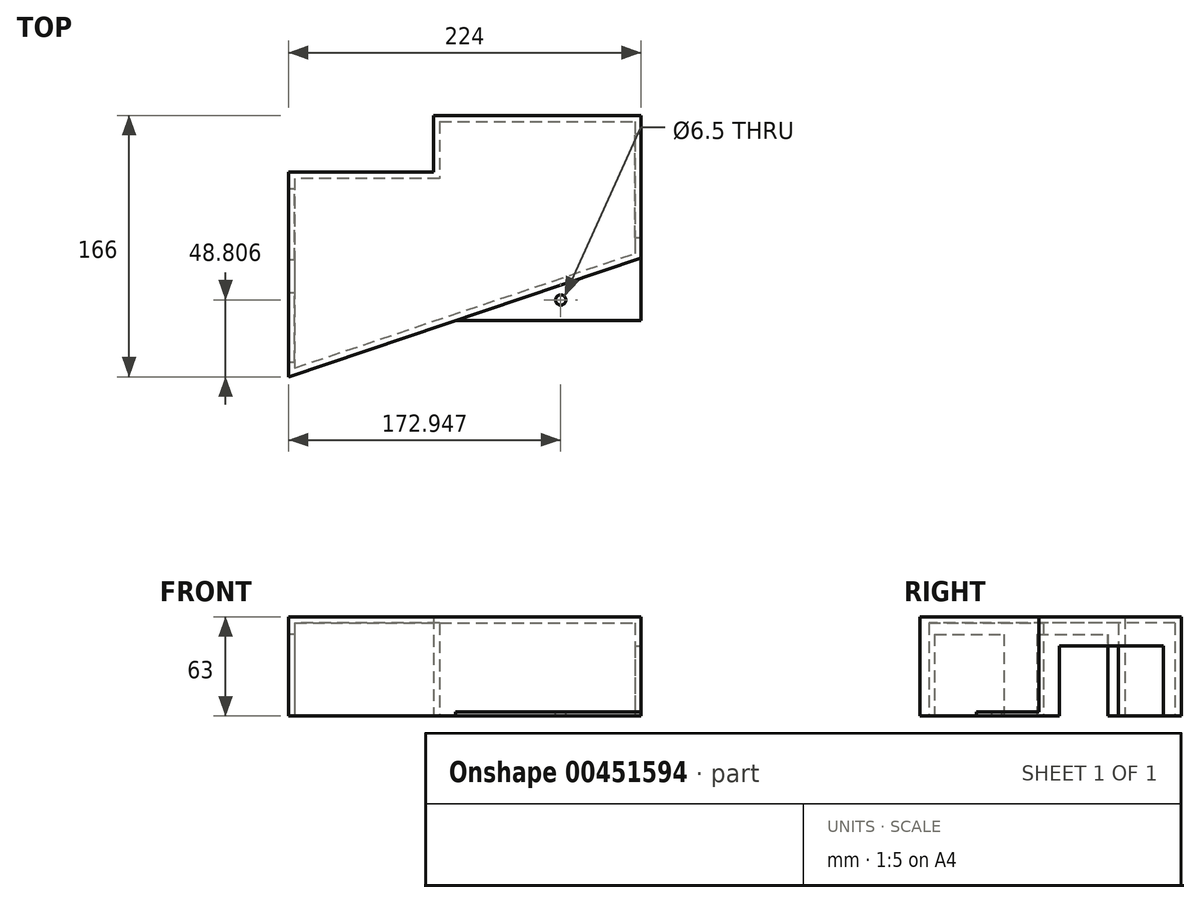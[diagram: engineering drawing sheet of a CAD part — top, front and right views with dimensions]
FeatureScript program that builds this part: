
annotation { "Feature Type Name" : "Feature", "Feature Type Description" : "" }
export const myFeature = defineFeature(function(context is Context, id is Id, definition is map)
    precondition{}
    {
        {
            var Q0;
            Q0=qCreatedBy(makeId("Top.planeOp"),FACE);
            var sketch = newSketch(context, id + "F0", { "sketchPlane" : qUnion([Q0])});
            skLineSegment(sketch, "E0.bottom", {"start": v(26.21, 65.96) * mm, "end": v(158.21, 65.96) * mm});
            skLineSegment(sketch, "E0.left", {"start": v(26.21, 65.96) * mm, "end": v(26.21, -24.04) * mm});
            skLineSegment(sketch, "E0.right", {"start": v(158.21, 65.96) * mm, "end": v(158.21, -24.56) * mm});
            skLineSegment(sketch, "E1", {"start": v(26.21, 65.96) * mm, "end": v(26.21, 29.96) * mm});
            skLineSegment(sketch, "E2", {"start": v(26.21, 29.96) * mm, "end": v(-65.79, 29.96) * mm});
            skLineSegment(sketch, "E3", {"start": v(-65.79, 29.96) * mm, "end": v(-65.79, -100.04) * mm});
            skLineSegment(sketch, "E4", {"start": v(26.21, -69.04) * mm, "end": v(26.21, -24.04) * mm});
            skLineSegment(sketch, "E5.0", {"start": v(40.46, -64.23) * mm, "end": v(158.13, -64.23) * mm});
            skLineSegment(sketch, "E6", {"start": v(158.13, -64.23) * mm, "end": v(158.21, -24.56) * mm});
            skLineSegment(sketch, "E7", {"start": v(-65.79, -100.04) * mm, "end": v(158.21, -24.56) * mm});
            skSolve(sketch);
        }
        {
            var Q0;
            Q0=makeQuery(id+"F0.imprint","IMPRINT",FACE,{"disambiguationData":[TD([[makeQuery(id+"F0.imprint","IMPRINT",EDGE,{"derivedFrom":sQuery(id+"F0.wireOp",EDGE,"E0.left")}),-1.0]])]});
            var Q1;
            Q1=makeQuery(id+"F0.imprint","IMPRINT",FACE,{"disambiguationData":[TD([[makeQuery(id+"F0.imprint","IMPRINT",EDGE,{"derivedFrom":sQuery(id+"F0.wireOp",EDGE,"E0.bottom")}),-1.0]])]});
            extrude(context, id + "F1", {"entities" : qUnion([Q0, Q1]), "depth" : 63 * mm});
        }
        {
            var Q0;
            Q0 = qSketchRegion(id + "F0", true);
            extrude(context, id + "F2", {"entities" : qUnion([Q0]), "operationType" : NewBodyOperationType.ADD, "depth" : 2.5 * mm});
        }
        {
            var Q0;
            {var subQ0=sQuery(id+"F0.wireOp",EDGE,"E3");var subQ1=sQuery(id+"F0.wireOp",EDGE,"E2");var subQ2=sQuery(id+"F0.wireOp",EDGE,"E1");var subQ3=sQuery(id+"F0.wireOp",EDGE,"E0.right");var subQ4=sQuery(id+"F0.wireOp",EDGE,"E0.bottom");Q0=makeQuery(id+"F2.boolean.opBoolean","MERGE",FACE,{"derivedFrom":[makeQuery(id+"F1.opExtrude","CAP_FACE",FACE,{"disambiguationData":[OSD([subQ4,sQuery(id+"F0.wireOp",EDGE,"E0.top"),subQ3,subQ2,subQ1,subQ0,sQuery(id+"F0.wireOp",EDGE,"OJzQ3pk2-BgUm-UeRg-AuBx-Udj2uWQ00Nrx"),sQuery(id+"F0.wireOp",EDGE,"URydDZTy-mC02-9x6z-TsWp-lHxEPAydHY93")])],"isStart":true}),makeQuery(id+"F2.opExtrude","CAP_FACE",FACE,{"disambiguationData":[OSD([subQ4,subQ3,subQ2,subQ1,subQ0,sQuery(id+"F0.wireOp",EDGE,"bc03a410-fdc1-470a-8368-dbfc4951a3a4.0"),sQuery(id+"F0.wireOp",EDGE,"bc03a410-fdc1-470a-8368-dbfc4951a3a4.1"),sQuery(id+"F0.wireOp",EDGE,"bc03a410-fdc1-470a-8368-dbfc4951a3a4.2"),sQuery(id+"F0.wireOp",EDGE,"HxJhJByZ-rJ53-OPf5-e96h-yF964EYC62Se"),sQuery(id+"F0.wireOp",EDGE,"OOmkvEby-ESTa-VR8m-9cLz-AsmgeBhRQe72")])],"isStart":true})]});}
            shell(context, id + "F3", {"entities" : qUnion([Q0]), "thickness" : 4 * mm});
        }
        {
            var Q0;
            Q0=makeQuery(id+"F1.opExtrude","SWEPT_FACE",FACE,{"disambiguationData":[OSD([sQuery(id+"F0.wireOp",EDGE,"E3")])]});
            var sketch = newSketch(context, id + "F4", { "sketchPlane" : qUnion([Q0])});
            skLineSegment(sketch, "E8.bottom", {"start": v(-19.17, 0) * mm, "end": v(25.83, 0) * mm});
            skLineSegment(sketch, "E8.top", {"start": v(-19.17, 52) * mm, "end": v(25.83, 52) * mm});
            skLineSegment(sketch, "E8.left", {"start": v(-19.17, 0) * mm, "end": v(-19.17, 52) * mm});
            skLineSegment(sketch, "E8.right", {"start": v(25.83, 0) * mm, "end": v(25.83, 52) * mm});
            skLineSegment(sketch, "E9", {"start": v(25.83, 0) * mm, "end": v(46.83, 0) * mm});
            skLineSegment(sketch, "E10.bottom", {"start": v(46.83, 0) * mm, "end": v(90.83, 0) * mm});
            skLineSegment(sketch, "E10.top", {"start": v(46.83, 52) * mm, "end": v(90.83, 52) * mm});
            skLineSegment(sketch, "E10.left", {"start": v(46.83, 0) * mm, "end": v(46.83, 52) * mm});
            skLineSegment(sketch, "E10.right", {"start": v(90.83, 0) * mm, "end": v(90.83, 52) * mm});
            skSolve(sketch);
        }
        {
            var Q0;
            Q0=makeQuery(id+"F4.imprint","IMPRINT",FACE,{"disambiguationData":[TD([[makeQuery(id+"F4.imprint","IMPRINT",EDGE,{"derivedFrom":sQuery(id+"F4.wireOp",EDGE,"E10.bottom")}),1.0]])]});
            var Q1;
            Q1=makeQuery(id+"F4.imprint","IMPRINT",FACE,{"disambiguationData":[TD([[makeQuery(id+"F4.imprint","IMPRINT",EDGE,{"derivedFrom":sQuery(id+"F4.wireOp",EDGE,"E8.bottom")}),1.0]])]});
            extrude(context, id + "F5", {"entities" : qUnion([Q0, Q1]), "operationType" : NewBodyOperationType.REMOVE, "oppositeDirection" : true, "depth" : 4.5 * mm});
        }
        {
            var Q0;
            Q0=makeQuery(id+"F1.opExtrude","SWEPT_FACE",FACE,{"disambiguationData":[OSD([sQuery(id+"F0.wireOp",EDGE,"E0.right")])]});
            var sketch = newSketch(context, id + "F6", { "sketchPlane" : qUnion([Q0])});
            skLineSegment(sketch, "E11.bottom", {"start": v(-11.54, 44.5) * mm, "end": v(54.46, 44.5) * mm});
            skLineSegment(sketch, "E11.top", {"start": v(-11.54, 0) * mm, "end": v(54.46, 0) * mm});
            skLineSegment(sketch, "E11.left", {"start": v(-11.54, 44.5) * mm, "end": v(-11.54, 0) * mm});
            skLineSegment(sketch, "E11.right", {"start": v(54.46, 44.5) * mm, "end": v(54.46, 0) * mm});
            skLineSegment(sketch, "E12", {"start": v(54.46, 44.5) * mm, "end": v(65.96, 44.5) * mm});
            skLineSegment(sketch, "E13", {"start": v(36.06, 44.5) * mm, "end": v(36.06, 63) * mm});
            skSolve(sketch);
        }
        {
            var Q0;
            Q0=makeQuery(id+"F6.imprint","IMPRINT",FACE,{"disambiguationData":[TD([[makeQuery(id+"F6.imprint","IMPRINT",EDGE,{"derivedFrom":sQuery(id+"F6.wireOp",EDGE,"E11.top")}),1.0]])]});
            var Q1;
            Q1=makeQuery(id+"F6.imprint","IMPRINT",FACE,{"disambiguationData":[TD([[makeQuery(id+"F6.imprint","IMPRINT",EDGE,{"derivedFrom":sQuery(id+"F6.wireOp",EDGE,"E11.top")}),-1.0]])]});
            extrude(context, id + "F7", {"entities" : qUnion([Q0, Q1]), "operationType" : NewBodyOperationType.REMOVE, "oppositeDirection" : true, "depth" : 5 * mm, "offsetDistance" : 25 * mm});
        }
        {
            var Q0;
            Q0=makeQuery(id+"F2.opExtrude","CAP_FACE",FACE,{"disambiguationData":[OSD([sQuery(id+"F0.wireOp",EDGE,"E0.bottom"),sQuery(id+"F0.wireOp",EDGE,"E0.right"),sQuery(id+"F0.wireOp",EDGE,"E1"),sQuery(id+"F0.wireOp",EDGE,"E2"),sQuery(id+"F0.wireOp",EDGE,"E3"),sQuery(id+"F0.wireOp",EDGE,"E5.0"),sQuery(id+"F0.wireOp",EDGE,"E6"),sQuery(id+"F0.wireOp",EDGE,"E7")])],"isStart":false});
            var sketch = newSketch(context, id + "F8", { "sketchPlane" : qUnion([Q0])});
            skCircle(sketch, "E14", {"center": v(107.16, -51.23) * mm, "radius": 3.25 * mm});
            skLineSegment(sketch, "E15", {"start": v(107.16, -51.23) * mm, "end": v(158.16, -51.23) * mm});
            skLineSegment(sketch, "E16", {"start": v(107.16, -51.23) * mm, "end": v(107.16, -64.23) * mm});
            skSolve(sketch);
        }
        {
            var Q0;
            {var subQ0=sQuery(id+"F8.wireOp",EDGE,"E15");var subQ1=sQuery(id+"F8.wireOp",EDGE,"E14");var subQ2=makeQuery(id+"F8.imprint","INTERSECT",VERTEX,{"derivedFrom":[subQ1,subQ0]});Q0=makeQuery(id+"F8.imprint","IMPRINT",FACE,{"disambiguationData":[TD([[makeQuery(id+"F8.imprint","IMPRINT",EDGE,{"disambiguationData":[TD([[subQ2,1.0]])],"derivedFrom":subQ1}),1.0]])]});}
            var Q1;
            {var subQ0=sQuery(id+"F8.wireOp",EDGE,"E15");var subQ1=sQuery(id+"F8.wireOp",EDGE,"E14");var subQ2=makeQuery(id+"F8.imprint","INTERSECT",VERTEX,{"derivedFrom":[subQ1,subQ0]});Q1=makeQuery(id+"F8.imprint","IMPRINT",FACE,{"disambiguationData":[TD([[makeQuery(id+"F8.imprint","IMPRINT",EDGE,{"disambiguationData":[TD([[subQ2,-1.0]])],"derivedFrom":subQ1}),1.0]])]});}
            extrude(context, id + "F9", {"entities" : qUnion([Q0, Q1]), "operationType" : NewBodyOperationType.REMOVE, "oppositeDirection" : true, "depth" : 25 * mm, "offsetDistance" : 25 * mm});
        }
    });
